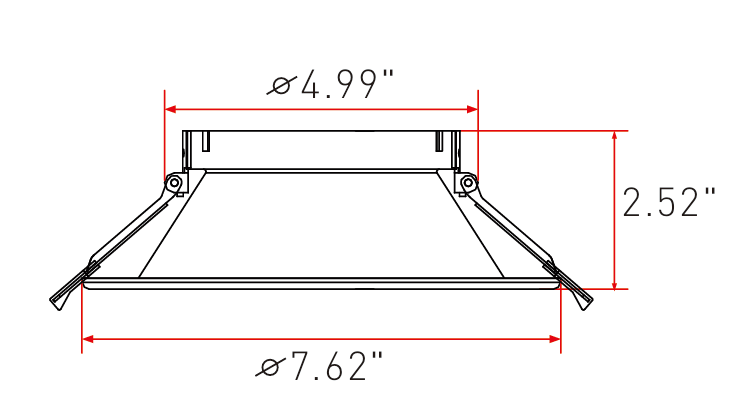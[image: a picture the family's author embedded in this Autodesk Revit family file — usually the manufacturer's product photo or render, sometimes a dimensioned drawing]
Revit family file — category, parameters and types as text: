
# Revit family: Alcon-14123-6R-Revit-Family
name_source: partatom
category: Lighting Fixtures
units: mm (PartAtom-declared; Revit-internal decimal feet)

## family parameters
Always vertical = Yes
Cut with Voids When Loaded = No
Host = Ceiling
Light Source = Yes
OmniClass Number = 23.80.70.11
OmniClass Title = Luminaries for Internal Lighting
Part Type = Normal
Room Calculation Point = No
Round Connector Dimension = Use Diameter
Shared = No

## types (1)
- Type 1
    Color Filter = 16777215
    Default Elevation = 0' - 0"
    Dimming Lamp Color Temperature Shift = <None>
    Housing = <By Category>
    Light Source Symbol Length = 10' - 0"
    LightSource = <By Category>
    Link To Product Page = https://www.alconlighting.com
    Manufacturer = Alcon Light
    Product Identity = Alcon Lighting 14123-6R
    Spot Beam Angle = 30.00°
    Spot Field Angle = 90.00°
    Tilt Angle = 60.00°

## geometry (parser evidence)
native form markers: Sweep x2
no freeform markers — native parametric forms only
